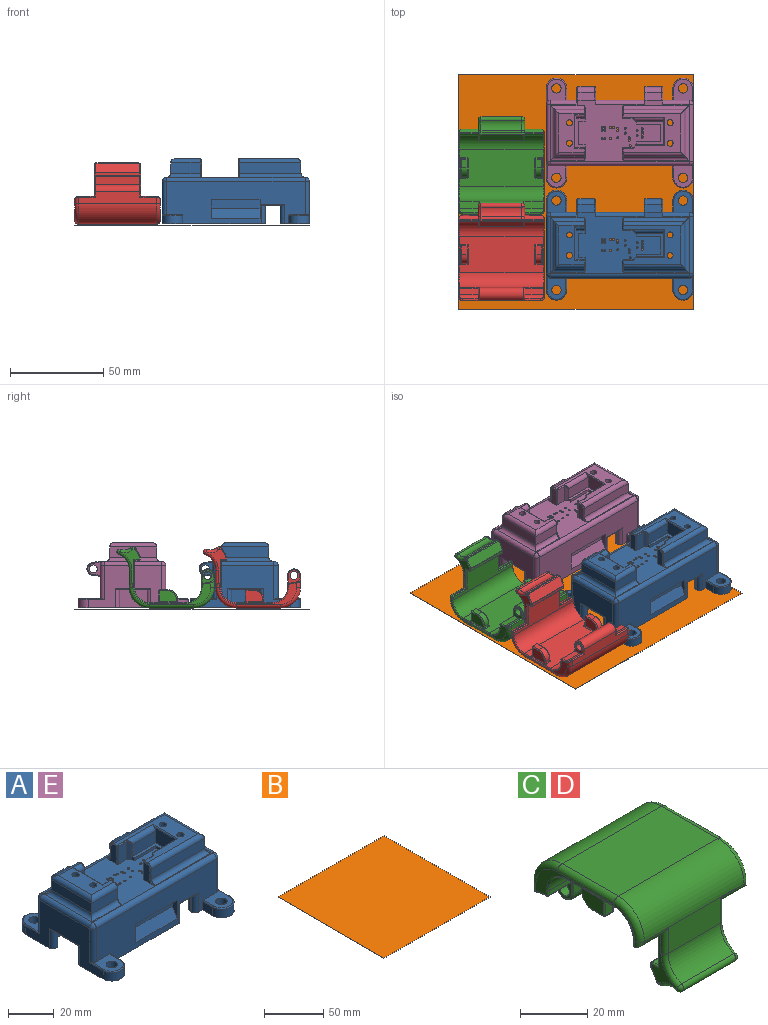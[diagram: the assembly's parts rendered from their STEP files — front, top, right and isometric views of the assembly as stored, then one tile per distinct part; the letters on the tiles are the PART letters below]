
ASSEMBLY  parts=5 mates=6
PART A: 216 faces, bbox 80x60x35.3 mm
  f0: cylinder r=2.25mm len=26.1mm, axis (-1,0,0), area 92mm2, adj f3,f8,f138,f145,f192,f201
  f1: cylinder r=2.25mm len=14.3mm, axis (-1,0,0), area 50.4mm2, adj f3,f8,f103,f139,f198
  f2: plane 74.5x22.75mm, normal (0,-1,0), area 1216.3mm2, adj f19,f21,f89,f91,f94,f96,f100,f107
  f3: plane 74.53x22.78mm, normal (0,1,0), area 1361.4mm2, adj f0,f1,f14,f19,f81,f82,f87,f88
  f4: plane 70x25.24mm, normal (0,0,-1), area 1712.8mm2, adj f12,f13,f17,f18,f41,f42,f43,f44
  f5: plane 14.57x6.25mm, normal (0,-1,0), area 91.1mm2, adj f6,f77,f118,f164
  f6: plane 13.46x8mm, normal (-1,0,0), area 101.4mm2, adj f5,f7,f77,f118,f174
  f7: plane 14.57x8mm, normal (0,1,0), area 116.6mm2, adj f6,f77,f175,f176
  f8: plane 74.63x33.12mm, normal (0,0,1), area 978.8mm2, adj f0,f1,f24,f28,f32,f33,f34,f35
  f9: plane 48x22.75mm, normal (-1,0,0), area 577.5mm2, adj f14,f21,f84,f93,f99,f100,f102,f123
  f10: plane 48x22.75mm, normal (1,0,0), area 777mm2, adj f19,f85,f90,f106,f107,f112,f204,f209
  f11: plane 10x0.5mm, normal (1,0,0), area 5mm2, adj f14,f78,f126,f127
  f12: plane 70x17mm, normal (0,-1,0), area 1058.8mm2, adj f4,f13,f14,f17,f19,f126,f131,f214
  f13: plane 25.24x17mm, normal (1,0,0), area 229.6mm2, adj f4,f12,f14,f18,f21,f123,f128,f211
  f14: plane 55.4x22.25mm, normal (0,0,-1), area 394.9mm2, adj f3,f9,f11,f12,f13,f81,f83,f84
  f15: plane 10x0.5mm, normal (-1,0,0), area 5mm2, adj f19,f79,f129,f130
  f16: plane 10x0.5mm, normal (-1,0,0), area 5mm2, adj f19,f78,f131,f132
  f17: plane 25.24x17mm, normal (-1,0,0), area 429.1mm2, adj f4,f12,f18,f19
  f18: plane 70x17mm, normal (0,1,0), area 1058.8mm2, adj f4,f13,f17,f19,f21,f124,f130,f213
  f19: plane 59x15.6mm, normal (0,0,-1), area 461.4mm2, adj f2,f3,f10,f12,f15,f16,f17,f18
  f20: plane 10x0.5mm, normal (1,0,0), area 5mm2, adj f21,f79,f124,f125
  f21: plane 55.4x22.25mm, normal (0,0,-1), area 394.9mm2, adj f2,f9,f13,f18,f20,f93,f95,f96
  f22: plane 25.24x5.5mm, normal (-1,0,0), area 138.8mm2, adj f23,f29,f101,f120
  f23: plane 15.9x5.5mm, normal (0,-1,0), area 87.5mm2, adj f22,f98,f121,f162
  f24: plane 9.5x6.87mm, normal (1,0,0), area 38.3mm2, adj f8,f68,f71,f158,f160,f161,f162,f163
  f25: plane 8x4.5mm, normal (0,1,0), area 36mm2, adj f26,f71,f157,f158
  f26: plane 16.68x8mm, normal (1,0,0), area 127.2mm2, adj f25,f27,f71,f122,f156
  f27: plane 6.25x4.5mm, normal (0,-1,0), area 28.1mm2, adj f26,f71,f122,f155
  f28: plane 9.5x6.87mm, normal (1,0,0), area 37.6mm2, adj f8,f70,f71,f150,f151,f152,f153,f154
  f29: plane 15.9x5.5mm, normal (0,1,0), area 87.5mm2, adj f22,f97,f119,f151
  f30: plane 20.74x13.65mm, normal (0,0,1), area 174.1mm2, adj f66,f67,f119,f120,f121,f122,f153,f156
  f31: plane 33.1x5.5mm, normal (0,1,0), area 182.1mm2, adj f39,f111,f115,f167
  f32: plane 9.5x4.87mm, normal (-1,0,0), area 35.3mm2, adj f8,f165,f167,f169,f170,f172,f173
  f33: plane 9.49x5.25mm, normal (0,-1,0), area 49.9mm2, adj f8,f34,f166,f168,f169
  f34: plane 9.48x1.61mm, normal (-0.71,-0.71,0), area 19mm2, adj f8,f33,f73,f77,f164,f166
  f35: plane 9.5x1.61mm, normal (-0.71,0.71,0), area 20mm2, adj f8,f36,f72,f77,f175,f178
  f36: plane 9.5x5.25mm, normal (0,1,0), area 49.9mm2, adj f8,f35,f179,f180
  f37: plane 9.5x4.87mm, normal (-1,0,0), area 35.3mm2, adj f8,f179,f182,f183,f184,f185
  f38: plane 33.1x5.5mm, normal (0,-1,0), area 182.1mm2, adj f39,f114,f117,f184
  f39: plane 25.24x5.5mm, normal (1,0,0), area 138.8mm2, adj f31,f38,f113,f116
  f40: plane 30.85x20.74mm, normal (0,0,1), area 273.4mm2, adj f64,f65,f115,f116,f117,f118,f172,f174
  f41: cylinder r=0.55mm len=8mm, axis (0,0,1), area 27.6mm2, adj f4,f8
  f42: cylinder r=0.55mm len=8mm, axis (0,0,1), area 27.6mm2, adj f4,f8
  f43: cylinder r=0.55mm len=8mm, axis (0,0,1), area 27.6mm2, adj f4,f8
  f44: cylinder r=0.55mm len=8mm, axis (0,0,1), area 27.6mm2, adj f4,f8
  f45: cylinder r=0.55mm len=8mm, axis (0,0,1), area 27.6mm2, adj f4,f8
  f46: cylinder r=0.55mm len=8mm, axis (0,0,1), area 27.6mm2, adj f4,f8
  f47: cylinder r=0.55mm len=8mm, axis (0,0,1), area 27.6mm2, adj f4,f8
  f48: cylinder r=0.55mm len=8mm, axis (0,0,1), area 27.6mm2, adj f4,f8
  f49: cylinder r=0.55mm len=8mm, axis (0,0,1), area 27.6mm2, adj f4,f8
  f50: cylinder r=0.55mm len=8mm, axis (0,0,1), area 27.6mm2, adj f4,f8
  f51: cylinder r=0.55mm len=8mm, axis (0,0,1), area 27.6mm2, adj f4,f8
  f52: cylinder r=0.55mm len=8mm, axis (0,0,1), area 27.6mm2, adj f4,f8
  f53: cylinder r=0.55mm len=8mm, axis (0,0,1), area 27.6mm2, adj f4,f8
  f54: cylinder r=0.55mm len=8mm, axis (0,0,1), area 27.6mm2, adj f4,f8
  f55: cylinder r=0.55mm len=8mm, axis (0,0,1), area 27.6mm2, adj f4,f8
  f56: cylinder r=0.55mm len=8mm, axis (0,0,1), area 27.6mm2, adj f4,f8
  f57: cylinder r=0.55mm len=8mm, axis (0,0,1), area 27.6mm2, adj f4,f8
  f58: cylinder r=0.55mm len=8mm, axis (0,0,1), area 27.6mm2, adj f4,f8
  f59: cylinder r=0.55mm len=8mm, axis (0,0,1), area 27.6mm2, adj f4,f8
  f60: cylinder r=0.55mm len=8mm, axis (0,0,1), area 27.6mm2, adj f4,f8
  f61: cylinder r=0.55mm len=8mm, axis (0,0,1), area 27.6mm2, adj f4,f8
  f62: cylinder r=0.55mm len=8mm, axis (0,0,1), area 27.6mm2, adj f4,f8
  f63: cylinder r=0.55mm len=8mm, axis (0,0,1), area 27.6mm2, adj f4,f8
  f64: cylinder r=1.6mm len=18mm, axis (0,0,1), area 181mm2, adj f4,f40
  f65: cylinder r=1.6mm len=18mm, axis (0,0,1), area 181mm2, adj f4,f40
  f66: cylinder r=1.6mm len=18mm, axis (0,0,1), area 181mm2, adj f4,f30
  f67: cylinder r=1.6mm len=18mm, axis (0,0,1), area 181mm2, adj f4,f30
  f68: plane 3.5x1.5mm, normal (0,1,0), area 5.2mm2, adj f8,f24,f69,f71
  f69: plane 12.84x1.5mm, normal (1,0,0), area 19.3mm2, adj f8,f68,f70,f71
  f70: plane 3.5x1.5mm, normal (0,-1,0), area 5.2mm2, adj f8,f28,f69,f71
  f71: plane 16.84x5mm, normal (0,0,1), area 34.4mm2, adj f24,f25,f26,f27,f28,f68,f69,f70
  f72: plane 1.5x1.5mm, normal (-1,0,0), area 2.2mm2, adj f8,f35,f76,f77
  f73: plane 1.5x1.5mm, normal (-1,0,0), area 2.2mm2, adj f8,f34,f74,f77
  f74: plane 13.28x1.5mm, normal (0,-1,0), area 19.9mm2, adj f8,f73,f75,f77
  f75: plane 9.62x1.5mm, normal (-1,0,0), area 14.4mm2, adj f8,f74,f76,f77
  f76: plane 13.28x1.5mm, normal (0,1,0), area 19.9mm2, adj f8,f72,f75,f77
  f77: plane 14.92x12.91mm, normal (0,0,1), area 58.8mm2, adj f5,f6,f7,f34,f35,f72,f73,f74
  f78: plane 9.67x4mm, normal (0,0,-1), area 33.8mm2, adj f11,f16,f126,f127,f131,f132,f214,f215
  f79: plane 9.67x4mm, normal (0,0,-1), area 33.8mm2, adj f15,f20,f124,f125,f129,f130,f212,f213
  f80: plane 16.17x3.5mm, normal (0,0,-1), area 52.5mm2, adj f123,f128,f210,f211
  f81: plane 6.38x4.5mm, normal (1,0,0), area 28.7mm2, adj f3,f14,f84,f191
  f82: plane 12.22x10mm, normal (0,0,1), area 83.9mm2, adj f3,f83,f99,f189,f190,f191
  f83: cylinder r=2.5mm len=5mm, axis (0,0,1), area 78.5mm2, adj f14,f82
  f84: cylinder r=5.5mm len=11mm, axis (0,0,1), area 77.8mm2, adj f9,f14,f81,f190
  f85: cylinder r=5.5mm len=11mm, axis (0,0,1), area 77.8mm2, adj f10,f19,f87,f208
  f86: cylinder r=2.5mm len=5mm, axis (0,0,1), area 78.5mm2, adj f19,f88
  f87: plane 6.38x4.5mm, normal (-1,0,0), area 28.7mm2, adj f3,f19,f85,f207
  f88: plane 12.22x10mm, normal (0,0,1), area 83.9mm2, adj f3,f86,f106,f207,f208,f209
  f89: plane 6.38x4.5mm, normal (-1,0,0), area 28.7mm2, adj f2,f19,f90,f206
  f90: cylinder r=5.5mm len=11mm, axis (0,0,1), area 77.8mm2, adj f10,f19,f89,f205
  f91: plane 12.22x10mm, normal (0,0,1), area 83.9mm2, adj f2,f92,f107,f204,f205,f206
  f92: cylinder r=2.5mm len=5mm, axis (0,0,1), area 78.5mm2, adj f19,f91
  f93: cylinder r=5.5mm len=11mm, axis (0,0,1), area 77.8mm2, adj f9,f21,f96,f187
  f94: plane 12.22x10mm, normal (0,0,1), area 83.9mm2, adj f2,f95,f100,f186,f187,f188
  f95: cylinder r=2.5mm len=5mm, axis (0,0,1), area 78.5mm2, adj f21,f94
  f96: plane 6.38x4.5mm, normal (1,0,0), area 28.7mm2, adj f2,f21,f93,f188
  f97: cylinder r=2.25mm len=18.15mm, axis (-1,0,0), area 60.2mm2, adj f8,f29,f101,f150
  f98: cylinder r=2.25mm len=18.15mm, axis (1,0,0), area 60.2mm2, adj f8,f23,f101,f163
  f99: cylinder r=2.25mm len=18.25mm, axis (0,0,-1), area 63.1mm2, adj f3,f9,f82,f103,f189
  f100: cylinder r=2.25mm len=18.25mm, axis (0,0,1), area 63.1mm2, adj f2,f9,f94,f104,f186
  f101: cylinder r=2.25mm len=29.74mm, axis (0,-1,0), area 97.2mm2, adj f22,f97,f98,f102
  f102: cylinder r=2.25mm len=30.74mm, axis (0,-1,0), area 108.6mm2, adj f8,f9,f101,f103,f104
  f103: sphere r=2.25mm, area 10.8mm2, adj f1,f99,f102
  f104: sphere r=2.25mm, area 8mm2, adj f100,f102,f108
  f105: cylinder r=2.25mm len=14.3mm, axis (-1,0,0), area 50.4mm2, adj f3,f8,f109,f144,f195
  f106: cylinder r=2.25mm len=18.25mm, axis (0,0,1), area 63.1mm2, adj f3,f10,f88,f109,f209
  f107: cylinder r=2.25mm len=18.25mm, axis (0,0,-1), area 63.1mm2, adj f2,f10,f91,f110,f204
  f108: cylinder r=2.25mm len=74.5mm, axis (1,0,0), area 263.3mm2, adj f2,f8,f104,f110
  f109: sphere r=2.25mm, area 5.1mm2, adj f105,f106,f112
  f110: sphere r=2.25mm, area 8mm2, adj f107,f108,f112
  f111: cylinder r=2.25mm len=35.35mm, axis (-1,0,0), area 121mm2, adj f8,f31,f113,f165
  f112: cylinder r=2.25mm len=30.74mm, axis (0,1,0), area 108.6mm2, adj f8,f10,f109,f110,f113
  f113: cylinder r=2.25mm len=29.74mm, axis (0,1,0), area 97.2mm2, adj f39,f111,f112,f114
  f114: cylinder r=2.25mm len=35.35mm, axis (1,0,0), area 121mm2, adj f8,f38,f113,f185
  f115: cylinder r=2.25mm len=33.1mm, axis (1,0,0), area 113mm2, adj f31,f40,f116,f170
  f116: cylinder r=2.25mm len=25.24mm, axis (0,-1,0), area 81.3mm2, adj f39,f40,f115,f117
  f117: cylinder r=2.25mm len=33.1mm, axis (-1,0,0), area 113mm2, adj f38,f40,f116,f183
  f118: cylinder r=2.25mm len=22.14mm, axis (1,0,0), area 55.1mm2, adj f5,f6,f40,f166,f168,f173,f174
  f119: cylinder r=2.25mm len=15.9mm, axis (1,0,0), area 52.2mm2, adj f29,f30,f120,f152
  f120: cylinder r=2.25mm len=25.24mm, axis (0,1,0), area 81.3mm2, adj f22,f30,f119,f121
  f121: cylinder r=2.25mm len=15.9mm, axis (-1,0,0), area 52.2mm2, adj f23,f30,f120,f161
  f122: cylinder r=2.25mm len=5mm, axis (-1,0,0), area 16.3mm2, adj f26,f27,f30,f154,f156
  f123: cylinder r=2.25mm len=10.5mm, axis (0,0,-1), area 71.5mm2, adj f9,f13,f21,f80,f210,f211
  f124: cylinder r=2.25mm len=10.5mm, axis (0,0,1), area 35.7mm2, adj f18,f20,f21,f79,f213
  f125: cylinder r=2.25mm len=10.5mm, axis (0,0,-1), area 35.7mm2, adj f2,f20,f21,f79,f212
  f126: cylinder r=2.25mm len=10.5mm, axis (0,0,-1), area 35.7mm2, adj f11,f12,f14,f78,f214
  f127: cylinder r=2.25mm len=10.5mm, axis (0,0,1), area 35.7mm2, adj f3,f11,f14,f78,f215
  f128: cylinder r=2.25mm len=10.5mm, axis (0,0,1), area 71.5mm2, adj f9,f13,f14,f80,f210,f211
  f129: cylinder r=2.25mm len=10.5mm, axis (0,0,1), area 35.7mm2, adj f2,f15,f19,f79,f212
  f130: cylinder r=2.25mm len=10.5mm, axis (0,0,-1), area 35.7mm2, adj f15,f18,f19,f79,f213
  f131: cylinder r=2.25mm len=10.5mm, axis (0,0,1), area 35.7mm2, adj f12,f16,f19,f78,f214
  f132: cylinder r=2.25mm len=10.5mm, axis (0,0,-1), area 35.7mm2, adj f3,f16,f19,f78,f215
  f133: plane 26x5.2mm, normal (0,-0.87,0.5), area 156mm2, adj f2,f134,f136,f137
  f134: plane 26x4.8mm, normal (0,-1,0), area 124.8mm2, adj f133,f135,f136,f137
  f135: plane 26x3mm, normal (0,0,-1), area 78mm2, adj f2,f134,f136,f137
  f136: plane 10x3mm, normal (-1,0,0), area 22.2mm2, adj f2,f133,f134,f135
  f137: plane 10x3mm, normal (1,0,0), area 22.2mm2, adj f2,f133,f134,f135
  f138: plane 7.71x7.12mm, normal (1,0,0), area 24.9mm2, adj f0,f3,f143,f201,f202,f203
  f139: plane 7.71x7.12mm, normal (-1,0,0), area 24.9mm2, adj f1,f3,f143,f198,f199,f200
  f140: plane 9x4.14mm, normal (0,0.13,-0.99), area 37.6mm2, adj f3,f141,f200,f203
  f141: cylinder r=3.5mm len=9mm, axis (-1,0,0), area 91mm2, adj f140,f142,f199,f202
  f142: plane 9x4.14mm, normal (0,0.13,0.99), area 37.6mm2, adj f8,f141,f198,f201
  f143: cylinder r=2.1mm len=10mm, axis (-1,0,0), area 131.9mm2, adj f138,f139
  f144: plane 7.71x7.12mm, normal (1,0,0), area 24.9mm2, adj f3,f105,f149,f195,f196,f197
  f145: plane 7.71x7.12mm, normal (-1,0,0), area 24.9mm2, adj f0,f3,f149,f192,f193,f194
  f146: plane 9x4.14mm, normal (0,0.13,-0.99), area 37.6mm2, adj f3,f147,f194,f197
  f147: cylinder r=3.5mm len=9mm, axis (-1,0,0), area 91mm2, adj f146,f148,f193,f196
  f148: plane 9x4.14mm, normal (0,0.13,0.99), area 37.6mm2, adj f8,f147,f192,f195
  f149: cylinder r=2.1mm len=10mm, axis (-1,0,0), area 131.9mm2, adj f144,f145
  f150: torus R=2.75mm, axis (-1,0,0), area 2.4mm2, adj f8,f28,f97,f151
  f151: cylinder r=0.5mm len=5.5mm, axis (0,0,1), area 4.3mm2, adj f28,f29,f150,f152
  f152: torus R=1.75mm, axis (-1,0,0), area 2.6mm2, adj f28,f119,f151,f153
  f153: cylinder r=0.5mm len=0.5mm, axis (0,-1,0), area 0.2mm2, adj f28,f30,f152,f154
  f154: torus R=1.75mm, axis (-1,0,0), area 2.6mm2, adj f28,f122,f153,f155
  f155: cylinder r=0.5mm len=6.25mm, axis (0,0,-1), area 4.9mm2, adj f27,f28,f71,f154
  f156: cylinder r=0.5mm len=18.59mm, axis (0,-1,0), area 13.8mm2, adj f26,f30,f122,f157
  f157: cylinder r=0.5mm len=5mm, axis (1,0,0), area 3.7mm2, adj f25,f30,f156,f159
  f158: cylinder r=0.5mm len=8mm, axis (0,0,-1), area 6.3mm2, adj f24,f25,f71,f159
  f159: sphere r=0.5mm, area 0.2mm2, adj f157,f158,f160
  f160: cylinder r=0.5mm len=1.95mm, axis (0,-1,0), area 1.5mm2, adj f24,f30,f159,f161
  f161: torus R=1.75mm, axis (1,0,0), area 2.6mm2, adj f24,f121,f160,f162
  f162: cylinder r=0.5mm len=5.5mm, axis (0,0,1), area 4.3mm2, adj f23,f24,f161,f163
  f163: torus R=2.75mm, axis (1,0,0), area 2.4mm2, adj f8,f24,f98,f162
  f164: cylinder r=0.5mm len=6.25mm, axis (0,0,1), area 2.5mm2, adj f5,f34,f77,f166
  f165: torus R=2.75mm, axis (-1,0,0), area 2.4mm2, adj f8,f32,f111,f167
  f166: bspline ~2.24x2.07mm, area 1.8mm2, adj f33,f34,f118,f164,f168
  f167: cylinder r=0.5mm len=5.5mm, axis (0,0,-1), area 4.3mm2, adj f31,f32,f165,f170
  f168: cylinder r=0.5mm len=5.46mm, axis (1,0,0), area 4mm2, adj f33,f118,f166,f171
  f169: cylinder r=0.5mm len=9.49mm, axis (0,0,1), area 7.5mm2, adj f8,f32,f33,f171
  f170: torus R=1.75mm, axis (-1,0,0), area 2.6mm2, adj f32,f115,f167,f172
  f171: sphere r=0.5mm, area 0.2mm2, adj f168,f169,f173
  f172: cylinder r=0.5mm len=1.81mm, axis (0,1,0), area 1.4mm2, adj f32,f40,f170,f173
  f173: torus R=1.75mm, axis (-1,0,0), area 0.1mm2, adj f32,f118,f171,f172
  f174: cylinder r=0.5mm len=15.37mm, axis (0,-1,0), area 11.3mm2, adj f6,f40,f118,f176
  f175: cylinder r=0.5mm len=8mm, axis (0,0,1), area 3.1mm2, adj f7,f35,f77,f177
  f176: cylinder r=0.5mm len=15.07mm, axis (-1,0,0), area 11.6mm2, adj f7,f40,f174,f177
  f177: sphere r=0.5mm, area 0.1mm2, adj f175,f176,f178
  f178: cylinder r=0.5mm len=1.96mm, axis (0.71,0.71,0), area 1.7mm2, adj f35,f40,f177,f180
  f179: cylinder r=0.5mm len=9.5mm, axis (0,0,1), area 7.5mm2, adj f8,f36,f37,f181
  f180: cylinder r=0.5mm len=5.46mm, axis (1,0,0), area 4.2mm2, adj f36,f40,f178,f181
  f181: sphere r=0.5mm, area 0.5mm2, adj f179,f180,f182
  f182: cylinder r=0.5mm len=1.95mm, axis (0,1,0), area 1.5mm2, adj f37,f40,f181,f183
  f183: torus R=1.75mm, axis (1,0,0), area 2.6mm2, adj f37,f117,f182,f184
  f184: cylinder r=0.5mm len=5.5mm, axis (0,0,-1), area 4.3mm2, adj f37,f38,f183,f185
  f185: torus R=2.75mm, axis (1,0,0), area 2.4mm2, adj f8,f37,f114,f184
  f186: cylinder r=0.5mm len=8.63mm, axis (0,1,0), area 6.2mm2, adj f9,f94,f100,f187
  f187: torus R=5mm, axis (0,0,1), area 13.1mm2, adj f93,f94,f186,f188
  f188: cylinder r=0.5mm len=6.38mm, axis (0,1,0), area 5mm2, adj f2,f94,f96,f187
  f189: cylinder r=0.5mm len=8.63mm, axis (0,1,0), area 6.2mm2, adj f9,f82,f99,f190
  f190: torus R=5mm, axis (0,0,1), area 13.1mm2, adj f82,f84,f189,f191
  f191: cylinder r=0.5mm len=6.38mm, axis (0,1,0), area 5mm2, adj f3,f81,f82,f190
  f192: cylinder r=0.5mm len=6.42mm, axis (0,-0.99,0.13), area 4mm2, adj f0,f8,f145,f148,f193
  f193: torus R=3mm, axis (1,0,0), area 7.5mm2, adj f145,f147,f192,f194
  f194: cylinder r=0.5mm len=4.21mm, axis (0,0.99,0.13), area 3.3mm2, adj f3,f145,f146,f193
  f195: cylinder r=0.5mm len=6.42mm, axis (0,0.99,-0.13), area 4mm2, adj f8,f105,f144,f148,f196
  f196: torus R=3mm, axis (1,0,0), area 7.5mm2, adj f144,f147,f195,f197
  f197: cylinder r=0.5mm len=4.21mm, axis (0,-0.99,-0.13), area 3.3mm2, adj f3,f144,f146,f196
  f198: cylinder r=0.5mm len=6.42mm, axis (0,-0.99,0.13), area 4mm2, adj f1,f8,f139,f142,f199
  f199: torus R=3mm, axis (1,0,0), area 7.5mm2, adj f139,f141,f198,f200
  f200: cylinder r=0.5mm len=4.21mm, axis (0,0.99,0.13), area 3.3mm2, adj f3,f139,f140,f199
  f201: cylinder r=0.5mm len=6.42mm, axis (0,0.99,-0.13), area 4mm2, adj f0,f8,f138,f142,f202
  f202: torus R=3mm, axis (1,0,0), area 7.5mm2, adj f138,f141,f201,f203
  f203: cylinder r=0.5mm len=4.21mm, axis (0,-0.99,-0.13), area 3.3mm2, adj f3,f138,f140,f202
  f204: cylinder r=0.5mm len=8.63mm, axis (0,-1,0), area 6.2mm2, adj f10,f91,f107,f205
  f205: torus R=5mm, axis (0,0,1), area 13.1mm2, adj f90,f91,f204,f206
  f206: cylinder r=0.5mm len=6.38mm, axis (0,-1,0), area 5mm2, adj f2,f89,f91,f205
  f207: cylinder r=0.5mm len=6.38mm, axis (0,-1,0), area 5mm2, adj f3,f87,f88,f208
  f208: torus R=5mm, axis (0,0,1), area 13.1mm2, adj f85,f88,f207,f209
  f209: cylinder r=0.5mm len=8.63mm, axis (0,-1,0), area 6.2mm2, adj f10,f88,f106,f208
  f210: cylinder r=0.5mm len=19mm, axis (0,1,0), area 13.8mm2, adj f9,f80,f123,f128
  f211: cylinder r=0.5mm len=19mm, axis (0,-1,0), area 13.8mm2, adj f13,f80,f123,f128
  f212: cylinder r=0.5mm len=12.5mm, axis (-1,0,0), area 8.7mm2, adj f2,f79,f125,f129
  f213: cylinder r=0.5mm len=12.5mm, axis (1,0,0), area 8.7mm2, adj f18,f79,f124,f130
  f214: cylinder r=0.5mm len=12.5mm, axis (-1,0,0), area 8.7mm2, adj f12,f78,f126,f131
  f215: cylinder r=0.5mm len=12.5mm, axis (1,0,0), area 8.7mm2, adj f3,f78,f127,f132
PART B: 6 faces, bbox 126x126x0.1 mm
  f0: plane 126x0.1mm, normal (0,1,0), area 12.6mm2, adj f1,f3,f4,f5
  f1: plane 126x0.1mm, normal (-1,0,0), area 12.6mm2, adj f0,f2,f4,f5
  f2: plane 126x0.1mm, normal (0,-1,0), area 12.6mm2, adj f1,f3,f4,f5
  f3: plane 126x0.1mm, normal (1,0,0), area 12.6mm2, adj f0,f2,f4,f5
  f4: plane 126x126mm, normal (0,0,1), area 15876mm2, adj f0,f1,f2,f3
  f5: plane 126x126mm, normal (0,0,-1), area 15876mm2, adj f0,f1,f2,f3
PART C: 153 faces, bbox 46x53.1x33.8 mm
  f0: plane 10x3.54mm, normal (0,-0.13,-0.99), area 35.7mm2, adj f1,f31,f80,f86,f87
  f1: cylinder r=3.8mm len=10mm, axis (-1,0,0), area 24mm2, adj f0,f31,f71,f78,f81
  f2: plane 10.5x0.5mm, normal (0,0,-1), area 5.3mm2, adj f17,f27,f56,f102
  f3: plane 45x19.64mm, normal (0,0,-1), area 775.5mm2, adj f4,f15,f79,f82,f85,f88,f91,f93
  f4: cylinder r=8mm len=45mm, axis (-1,0,0), area 565.5mm2, adj f3,f5,f97,f136
  f5: plane 45x6.5mm, normal (0,-1,0), area 193.4mm2, adj f4,f29,f80,f86,f95,f123,f126,f134
  f6: plane 10x3.54mm, normal (0,-0.13,-0.99), area 35.7mm2, adj f7,f30,f123,f125,f126
  f7: cylinder r=3.8mm len=10mm, axis (-1,0,0), area 24mm2, adj f6,f30,f116,f119,f122
  f8: plane 42x6.5mm, normal (0,1,0), area 217.5mm2, adj f9,f29,f61,f67,f68,f71,f116,f117
  f9: cylinder r=11mm len=42mm, axis (-1,0,0), area 725.7mm2, adj f8,f10,f60,f66
  f10: plane 42x23.64mm, normal (0,0,1), area 992.9mm2, adj f9,f11,f59,f65
  f11: cylinder r=11mm len=42mm, axis (-1,0,0), area 725.7mm2, adj f10,f12,f58,f64
  f12: plane 42x9.38mm, normal (0,-1,0), area 210.5mm2, adj f11,f24,f44,f50,f56,f57,f62,f63
  f13: plane 10.5x0.5mm, normal (0,0,-1), area 5.3mm2, adj f16,f26,f62,f127
  f14: plane 45x14.7mm, normal (0,1,0), area 388.5mm2, adj f15,f23,f100,f102,f105,f124,f127,f130
  f15: cylinder r=8mm len=45mm, axis (-1,0,0), area 565.5mm2, adj f3,f14,f99,f135
  f16: plane 41.64x11.47mm, normal (1,0,0), area 70mm2, adj f13,f63,f64,f65,f66,f67,f122,f125
  f17: plane 41.64x11.47mm, normal (-1,0,0), area 70mm2, adj f2,f57,f58,f59,f60,f61,f81,f87
  f18: cylinder r=5mm len=22mm, axis (-1,0,0), area 121.7mm2, adj f19,f25,f47,f53
  f19: cylinder r=2mm len=22mm, axis (-1,0,0), area 31.8mm2, adj f18,f20,f48,f54
  f20: plane 22x0.71mm, normal (0,0,-1), area 15.6mm2, adj f19,f49,f55,f104
  f21: plane 24x4.83mm, normal (0,0.87,-0.5), area 133.4mm2, adj f101,f103,f104,f107,f110,f111
  f22: plane 24x1.37mm, normal (0,1,0), area 32.8mm2, adj f109,f110,f114,f115
  f23: plane 24x2.5mm, normal (0,0,1), area 60mm2, adj f14,f108,f114,f121
  f24: cylinder r=9mm len=22mm, axis (-1,0,0), area 235mm2, adj f12,f25,f45,f51
  f25: cylinder r=1.5mm len=22mm, axis (-1,0,0), area 103.7mm2, adj f18,f24,f46,f52
  f26: plane 18.26x10.57mm, normal (1,0,0), area 46.4mm2, adj f13,f50,f51,f53,f54,f55,f62,f111
  f27: plane 18.26x10.57mm, normal (-1,0,0), area 46.4mm2, adj f2,f44,f45,f47,f48,f49,f56,f103
  f28: cylinder r=2.1mm len=25mm, axis (-1,0,0), area 329.9mm2, adj f30,f31
  f29: cylinder r=3.5mm len=24mm, axis (-1,0,0), area 263.9mm2, adj f5,f8,f72,f120
  f30: plane 7.21x6mm, normal (1,0,0), area 22.5mm2, adj f6,f7,f28,f116,f117,f120,f123
  f31: plane 7.21x6mm, normal (-1,0,0), area 22.5mm2, adj f0,f1,f28,f68,f71,f72,f80
  f32: plane 5.8x3mm, normal (0,-1,0), area 17.4mm2, adj f74,f75,f88,f89
  f33: plane 4.5x3mm, normal (0,0,-1), area 13.5mm2, adj f34,f69,f75,f76
  f34: cylinder r=5mm len=5mm, axis (-1,0,0), area 23.6mm2, adj f33,f35,f73,f84
  f35: plane 3x1.3mm, normal (0,1,0), area 3.9mm2, adj f34,f77,f90,f91
  f36: plane 9x5.8mm, normal (1,0,0), area 47.9mm2, adj f69,f73,f74,f77,f79
  f37: plane 9x5.8mm, normal (-1,0,0), area 47.9mm2, adj f76,f84,f89,f90,f96
  f38: plane 5.8x3mm, normal (0,-1,0), area 17.4mm2, adj f128,f137,f138,f139
  f39: plane 4.5x3mm, normal (0,0,-1), area 13.5mm2, adj f40,f128,f133,f140
  f40: cylinder r=5mm len=5mm, axis (-1,0,0), area 23.6mm2, adj f39,f41,f141,f145
  f41: plane 3x1.3mm, normal (0,1,0), area 3.9mm2, adj f40,f146,f149,f152
  f42: plane 9x5.8mm, normal (1,0,0), area 47.9mm2, adj f133,f137,f141,f146,f147
  f43: plane 9x5.8mm, normal (-1,0,0), area 47.9mm2, adj f139,f140,f145,f148,f149
  f44: cylinder r=1.5mm len=9.18mm, axis (0,0,-1), area 18.9mm2, adj f12,f27,f45,f56
  f45: torus R=10.5mm, axis (1,0,0), area 26.7mm2, adj f24,f27,f44,f46
  f46: sphere r=1.5mm, area 7.1mm2, adj f25,f45,f47
  f47: torus R=6.5mm, axis (1,0,0), area 14.5mm2, adj f18,f27,f46,f48
  f48: torus R=0.5mm, axis (1,0,0), area 2.5mm2, adj f19,f27,f47,f49
  f49: cylinder r=1.5mm len=1.5mm, axis (0,1,0), area 2.2mm2, adj f20,f27,f48,f101
  f50: cylinder r=1.5mm len=9.18mm, axis (0,0,1), area 18.9mm2, adj f12,f26,f51,f62
  f51: torus R=10.5mm, axis (1,0,0), area 26.7mm2, adj f24,f26,f50,f52
  f52: sphere r=1.5mm, area 7.1mm2, adj f25,f51,f53
  f53: torus R=6.5mm, axis (1,0,0), area 14.5mm2, adj f18,f26,f52,f54
  f54: torus R=0.5mm, axis (1,0,0), area 2.5mm2, adj f19,f26,f53,f55
  f55: cylinder r=1.5mm len=1.5mm, axis (0,-1,0), area 2.2mm2, adj f20,f26,f54,f107
  f56: cylinder r=2mm len=12mm, axis (-1,0,0), area 32.2mm2, adj f2,f12,f27,f44,f57
  f57: cylinder r=2mm len=2.2mm, axis (0,0,-1), area 4.6mm2, adj f12,f17,f56,f58
  f58: torus R=9mm, axis (1,0,0), area 50.7mm2, adj f11,f17,f57,f59
  f59: cylinder r=2mm len=23.64mm, axis (0,-1,0), area 74.3mm2, adj f10,f17,f58,f60
  f60: torus R=9mm, axis (1,0,0), area 50.7mm2, adj f9,f17,f59,f61
  f61: cylinder r=2mm len=3.42mm, axis (0,0,1), area 9.5mm2, adj f8,f17,f60,f78
  f62: cylinder r=2mm len=12mm, axis (-1,0,0), area 32.2mm2, adj f12,f13,f26,f50,f63
  f63: cylinder r=2mm len=2.2mm, axis (0,0,1), area 4.6mm2, adj f12,f16,f62,f64
  f64: torus R=9mm, axis (1,0,0), area 50.7mm2, adj f11,f16,f63,f65
  f65: cylinder r=2mm len=23.64mm, axis (0,1,0), area 74.3mm2, adj f10,f16,f64,f66
  f66: torus R=9mm, axis (1,0,0), area 50.7mm2, adj f9,f16,f65,f67
  f67: cylinder r=2mm len=3.42mm, axis (0,0,-1), area 9.5mm2, adj f8,f16,f66,f119
  f68: cylinder r=0.5mm len=3.08mm, axis (0,0,1), area 2.2mm2, adj f8,f31,f71,f72
  f69: cylinder r=0.5mm len=4.5mm, axis (0,-1,0), area 3.5mm2, adj f33,f36,f70,f73
  f70: sphere r=0.5mm, area 0.4mm2, adj f69,f74,f75
  f71: cylinder r=0.5mm len=9mm, axis (-1,0,0), area 10.1mm2, adj f1,f8,f31,f68,f78
  f72: torus R=3mm, axis (1,0,0), area 8.2mm2, adj f29,f31,f68,f80
  f73: torus R=4.5mm, axis (1,0,0), area 5.9mm2, adj f34,f36,f69,f77
  f74: cylinder r=0.5mm len=5.8mm, axis (0,0,1), area 4.6mm2, adj f32,f36,f70,f82
  f75: cylinder r=0.5mm len=3mm, axis (1,0,0), area 2.4mm2, adj f32,f33,f70,f83
  f76: cylinder r=0.5mm len=4.5mm, axis (0,1,0), area 3.5mm2, adj f33,f37,f83,f84
  f77: cylinder r=0.5mm len=1.3mm, axis (0,0,-1), area 1mm2, adj f35,f36,f73,f85
  f78: bspline ~2.58x2.55mm, area 3mm2, adj f1,f61,f71,f81
  f79: cylinder r=0.5mm len=9mm, axis (0,1,0), area 7.1mm2, adj f3,f36,f82,f85
  f80: cylinder r=0.5mm len=4.72mm, axis (0,0,-1), area 3.5mm2, adj f0,f5,f31,f72,f86
  f81: torus R=4.3mm, axis (1,0,0), area 0.7mm2, adj f1,f17,f78,f87
  f82: torus R=1mm, axis (0,0,1), area 0.8mm2, adj f3,f74,f79,f88
  f83: sphere r=0.5mm, area 0.4mm2, adj f75,f76,f89
  f84: torus R=4.5mm, axis (1,0,0), area 5.9mm2, adj f34,f37,f76,f90
  f85: torus R=1mm, axis (0,0,1), area 0.8mm2, adj f3,f77,f79,f91
  f86: cylinder r=0.5mm len=10.5mm, axis (-1,0,0), area 7.4mm2, adj f0,f5,f80,f92
  f87: cylinder r=0.5mm len=3.61mm, axis (0,0.99,-0.13), area 2.8mm2, adj f0,f17,f81,f92
  f88: cylinder r=0.5mm len=3mm, axis (-1,0,0), area 2.4mm2, adj f3,f32,f82,f93
  f89: cylinder r=0.5mm len=5.8mm, axis (0,0,-1), area 4.6mm2, adj f32,f37,f83,f93
  f90: cylinder r=0.5mm len=1.3mm, axis (0,0,1), area 1mm2, adj f35,f37,f84,f94
  f91: cylinder r=0.5mm len=3mm, axis (1,0,0), area 2.4mm2, adj f3,f35,f85,f94
  f92: sphere r=0.5mm, area 0.4mm2, adj f86,f87,f95
  f93: torus R=1mm, axis (0,0,1), area 0.8mm2, adj f3,f88,f89,f96
  f94: torus R=1mm, axis (0,0,1), area 0.8mm2, adj f3,f90,f91,f96
  f95: cylinder r=0.5mm len=1.78mm, axis (0,0,-1), area 1.4mm2, adj f5,f17,f92,f97
  f96: cylinder r=0.5mm len=9mm, axis (0,-1,0), area 7.1mm2, adj f37,f93,f94,f98
  f97: torus R=8.5mm, axis (1,0,0), area 10.1mm2, adj f4,f17,f95,f98
  f98: cylinder r=0.5mm len=19.64mm, axis (0,1,0), area 15.4mm2, adj f3,f17,f96,f97,f99
  f99: torus R=8.5mm, axis (1,0,0), area 10.1mm2, adj f15,f17,f98,f100
  f100: cylinder r=0.5mm len=2.2mm, axis (0,0,1), area 1.6mm2, adj f14,f17,f99,f102
  f101: bspline ~1.5x1.5mm, area 1.3mm2, adj f21,f49,f103,f104
  f102: cylinder r=0.5mm len=11mm, axis (1,0,0), area 8.2mm2, adj f2,f14,f100,f105
  f103: cylinder r=0.5mm len=4.08mm, axis (0,0.5,0.87), area 3.5mm2, adj f21,f27,f101,f106
  f104: cylinder r=0.5mm len=22mm, axis (-1,0,0), area 11.5mm2, adj f20,f21,f101,f107
  f105: cylinder r=0.5mm len=13.5mm, axis (0,0,1), area 10.1mm2, adj f14,f27,f102,f108
  f106: sphere r=0.5mm, area 0.1mm2, adj f103,f109,f110
  f107: bspline ~1.5x1.5mm, area 1.3mm2, adj f21,f55,f104,f111
  f108: cylinder r=0.5mm len=3mm, axis (0,-1,0), area 2.1mm2, adj f23,f27,f105,f112
  f109: cylinder r=0.5mm len=1.37mm, axis (0,0,1), area 1.1mm2, adj f22,f27,f106,f112
  f110: cylinder r=0.5mm len=24mm, axis (-1,0,0), area 6.3mm2, adj f21,f22,f106,f113
  f111: cylinder r=0.5mm len=4.08mm, axis (0,-0.5,-0.87), area 3.5mm2, adj f21,f26,f107,f113
  f112: sphere r=0.5mm, area 0.4mm2, adj f108,f109,f114
  f113: sphere r=0.5mm, area 0.1mm2, adj f110,f111,f115
  f114: cylinder r=0.5mm len=24mm, axis (-1,0,0), area 18.8mm2, adj f22,f23,f112,f118
  f115: cylinder r=0.5mm len=1.37mm, axis (0,0,-1), area 1.1mm2, adj f22,f26,f113,f118
  f116: cylinder r=0.5mm len=9mm, axis (-1,0,0), area 10.1mm2, adj f7,f8,f30,f117,f119
  f117: cylinder r=0.5mm len=3.08mm, axis (0,0,-1), area 2.2mm2, adj f8,f30,f116,f120
  f118: sphere r=0.5mm, area 0.4mm2, adj f114,f115,f121
  f119: bspline ~2.58x2.27mm, area 3mm2, adj f7,f67,f116,f122
  f120: torus R=3mm, axis (1,0,0), area 8.2mm2, adj f29,f30,f117,f123
  f121: cylinder r=0.5mm len=3mm, axis (0,1,0), area 2.1mm2, adj f23,f26,f118,f124
  f122: torus R=4.3mm, axis (1,0,0), area 0.7mm2, adj f7,f16,f119,f125
  f123: cylinder r=0.5mm len=4.72mm, axis (0,0,1), area 3.5mm2, adj f5,f6,f30,f120,f126
  f124: cylinder r=0.5mm len=13.5mm, axis (0,0,-1), area 10.1mm2, adj f14,f26,f121,f127
  f125: cylinder r=0.5mm len=3.61mm, axis (0,-0.99,0.13), area 2.8mm2, adj f6,f16,f122,f129
  f126: cylinder r=0.5mm len=10.5mm, axis (-1,0,0), area 7.4mm2, adj f5,f6,f123,f129
  f127: cylinder r=0.5mm len=11mm, axis (1,0,0), area 8.2mm2, adj f13,f14,f124,f130
  f128: cylinder r=0.5mm len=3mm, axis (1,0,0), area 2.4mm2, adj f38,f39,f131,f132
  f129: sphere r=0.5mm, area 0.4mm2, adj f125,f126,f134
  f130: cylinder r=0.5mm len=2.2mm, axis (0,0,-1), area 1.6mm2, adj f14,f16,f127,f135
  f131: sphere r=0.5mm, area 0.4mm2, adj f128,f133,f137
  f132: sphere r=0.5mm, area 0.4mm2, adj f128,f139,f140
  f133: cylinder r=0.5mm len=4.5mm, axis (0,-1,0), area 3.5mm2, adj f39,f42,f131,f141
  f134: cylinder r=0.5mm len=1.78mm, axis (0,0,1), area 1.4mm2, adj f5,f16,f129,f136
  f135: torus R=8.5mm, axis (1,0,0), area 10.1mm2, adj f15,f16,f130,f143
  f136: torus R=8.5mm, axis (1,0,0), area 10.1mm2, adj f4,f16,f134,f143
  f137: cylinder r=0.5mm len=5.8mm, axis (0,0,1), area 4.6mm2, adj f38,f42,f131,f142
  f138: cylinder r=0.5mm len=3mm, axis (-1,0,0), area 2.4mm2, adj f3,f38,f142,f144
  f139: cylinder r=0.5mm len=5.8mm, axis (0,0,-1), area 4.6mm2, adj f38,f43,f132,f144
  f140: cylinder r=0.5mm len=4.5mm, axis (0,1,0), area 3.5mm2, adj f39,f43,f132,f145
  f141: torus R=4.5mm, axis (1,0,0), area 5.9mm2, adj f40,f42,f133,f146
  f142: torus R=1mm, axis (0,0,1), area 0.8mm2, adj f3,f137,f138,f147
  f143: cylinder r=0.5mm len=19.64mm, axis (0,-1,0), area 15.4mm2, adj f3,f16,f135,f136,f147
  f144: torus R=1mm, axis (0,0,1), area 0.8mm2, adj f3,f138,f139,f148
  f145: torus R=4.5mm, axis (1,0,0), area 5.9mm2, adj f40,f43,f140,f149
  f146: cylinder r=0.5mm len=1.3mm, axis (0,0,-1), area 1mm2, adj f41,f42,f141,f150
  f147: cylinder r=0.5mm len=9mm, axis (0,1,0), area 7.1mm2, adj f42,f142,f143,f150
  f148: cylinder r=0.5mm len=9mm, axis (0,-1,0), area 7.1mm2, adj f3,f43,f144,f151
  f149: cylinder r=0.5mm len=1.3mm, axis (0,0,1), area 1mm2, adj f41,f43,f145,f151
  f150: torus R=1mm, axis (0,0,1), area 0.8mm2, adj f3,f146,f147,f152
  f151: torus R=1mm, axis (0,0,1), area 0.8mm2, adj f3,f148,f149,f152
  f152: cylinder r=0.5mm len=3mm, axis (1,0,0), area 2.4mm2, adj f3,f41,f150,f151
PART D: same geometry as C
PART E: same geometry as A
PLACE A t=(0.5,-28.61,25.65)mm
PLACE B t=(-1.75,0.51,0)mm
PLACE C rot(axis=(1,0,0),180deg) t=(-63,12.9,14.12)mm
PLACE D rot(axis=(1,0,0),180deg) t=(-63,-33.45,14.12)mm
PLACE E t=(0.5,31.61,25.65)mm
MATE planar A.f10 <-> E.f10  axis (1,0,0) through (63,-28.61,11.11)mm
MATE planar B.f3 <-> A.f10  axis (1,0,0) through (63,0,0.05)mm
MATE planar B.f1 <-> D.f17  axis (-1,0,0) through (-63,0,0.05)mm
MATE planar C.f37 <-> D.f37  axis (-1,0,0) through (-62,13.21,6.85)mm
MATE planar A.f85 <-> E.f85  axis (0,0,1) through (57.5,-4.61,0.65)mm
MATE planar D.f10 <-> C.f10  axis (0,0,-1) through (-40,-35.45,0.62)mm
